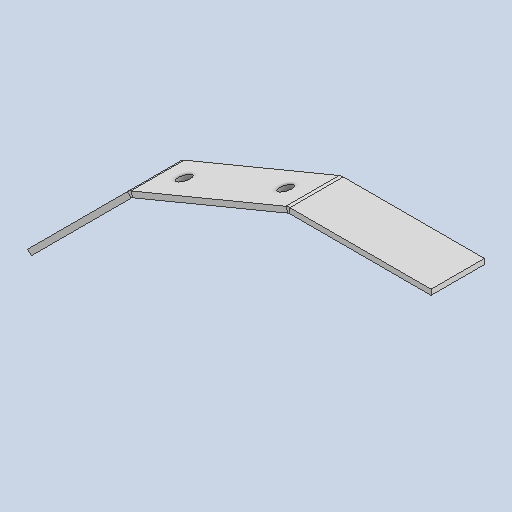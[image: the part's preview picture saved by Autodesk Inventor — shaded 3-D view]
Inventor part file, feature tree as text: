
AUTODESK INVENTOR PART (.ipt)
format: ipt  version: 2025 (Build 290162010, 162A)  size: 135,680 bytes
history: native  units: mm
features: sheet_metal_op x3, sketch x2, extrude x1, other x1
ambient origin geometry x8: Origin, YZ Plane, XZ Plane, XY Plane, X Axis, Y Axis, Z Axis, Center Point
bodies: Solid1 (feature_tree)
feature tree (7):
  sheet_metal_op  "Contour Flange1"
  extrude  "Extrusion1"  Depth=5.0mm
  sketch  "Sketch2"  dims[d0=513.0mm d1=260.0mm d2=635.0mm d6=5.0mm]
  other  "Plate1"
  sheet_metal_op  "Bend1"
  sheet_metal_op  "Corner1"
  sketch  "Sketch3"  dims[d10=5.0mm d14=5.0mm d15=16.0mm d16=8.0mm d17=8.0mm d18=4.0mm d19=16.0mm d20=8.0mm d21=80.0mm d22=8.0mm d23=8.0mm d24=32.0mm d25=8.0mm d26=8.0mm d27=20.0mm d28=82.5mm d30=0.0mm d31=0.0mm]
